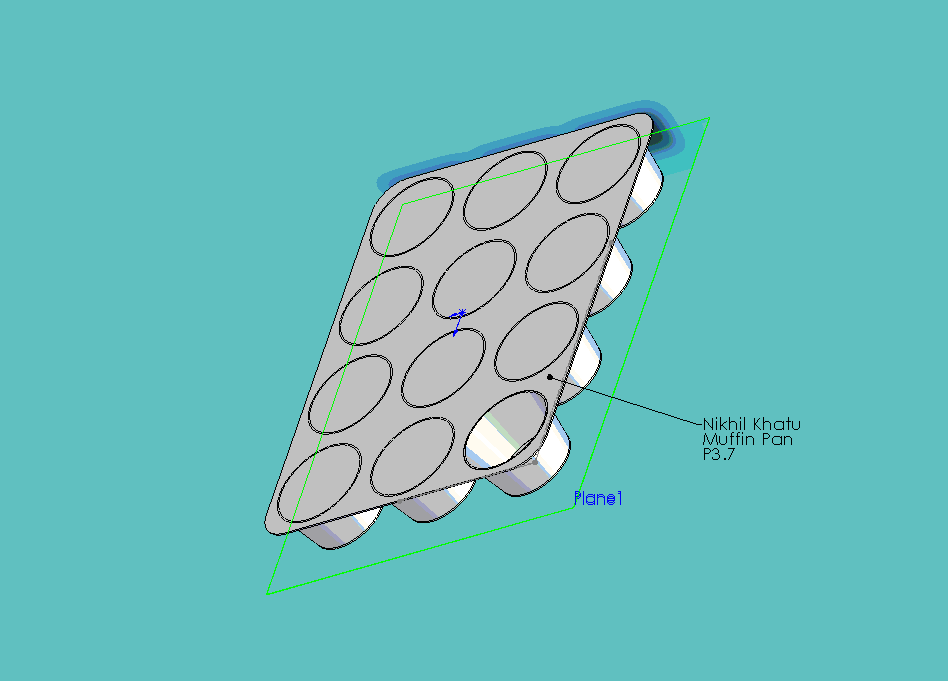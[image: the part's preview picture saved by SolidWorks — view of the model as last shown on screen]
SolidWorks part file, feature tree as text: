
SOLIDWORKS PART (.sldprt)
format: sldprt  version: not decoded by parser v0  size: 851,968 bytes
history: native  units: mm
features: sketch x5, plane x4, fillet x4, extrude x2, material x1, cut_extrude x1, shell x1, pattern_linear x1 (+11 scaffold rows collapsed)
feature tree (30):
  scaffold x11  (default folders/planes/origin — collapsed)
  material  "Material <not specified>"
  plane  "Frontal"
  plane  "Horizontal"
  plane  "Profile"
  sketch  "Sketch1"  dims[D1=266.7mm D2=355.6mm]
  extrude  "Extrude1"  Depth=1.27mm
  sketch  "Sketch2"  dims[D1=44.45mm D2=88.9mm D3=88.9mm D4=88.9mm D5=44.45mm D6=88.9mm D7=88.9mm]
  plane  "Plane1"  Offset=38.1mm
  sketch  "Sketch4"
  cut_extrude  "Cut-Extrude8"  Depth=1.27mm
  sketch  "Sketch5"  dims[D1=~23.250133mm]
  extrude  "Extrude2"  Depth=1.27mm
  shell  "Shell2"  Thickness=1.27mm
  sketch  "Sketch9"
  pattern_linear  "LPattern5"  Count1=4 Count2=3 Spacing1=88.9mm Spacing2=88.9mm
  fillet  "Fillet1"  Radius=25.4mm
  fillet  "Fillet2"  Radius=25.4mm
  fillet  "Fillet3"  Radius=25.4mm
  fillet  "Fillet4"  Radius=25.4mm
decode coverage: 12 of 14 modeling features carry decoded parameters
note: ~ marks probable driven/reference dimensions
note: suppression state not decoded; provenance and decode notes live in map.json
